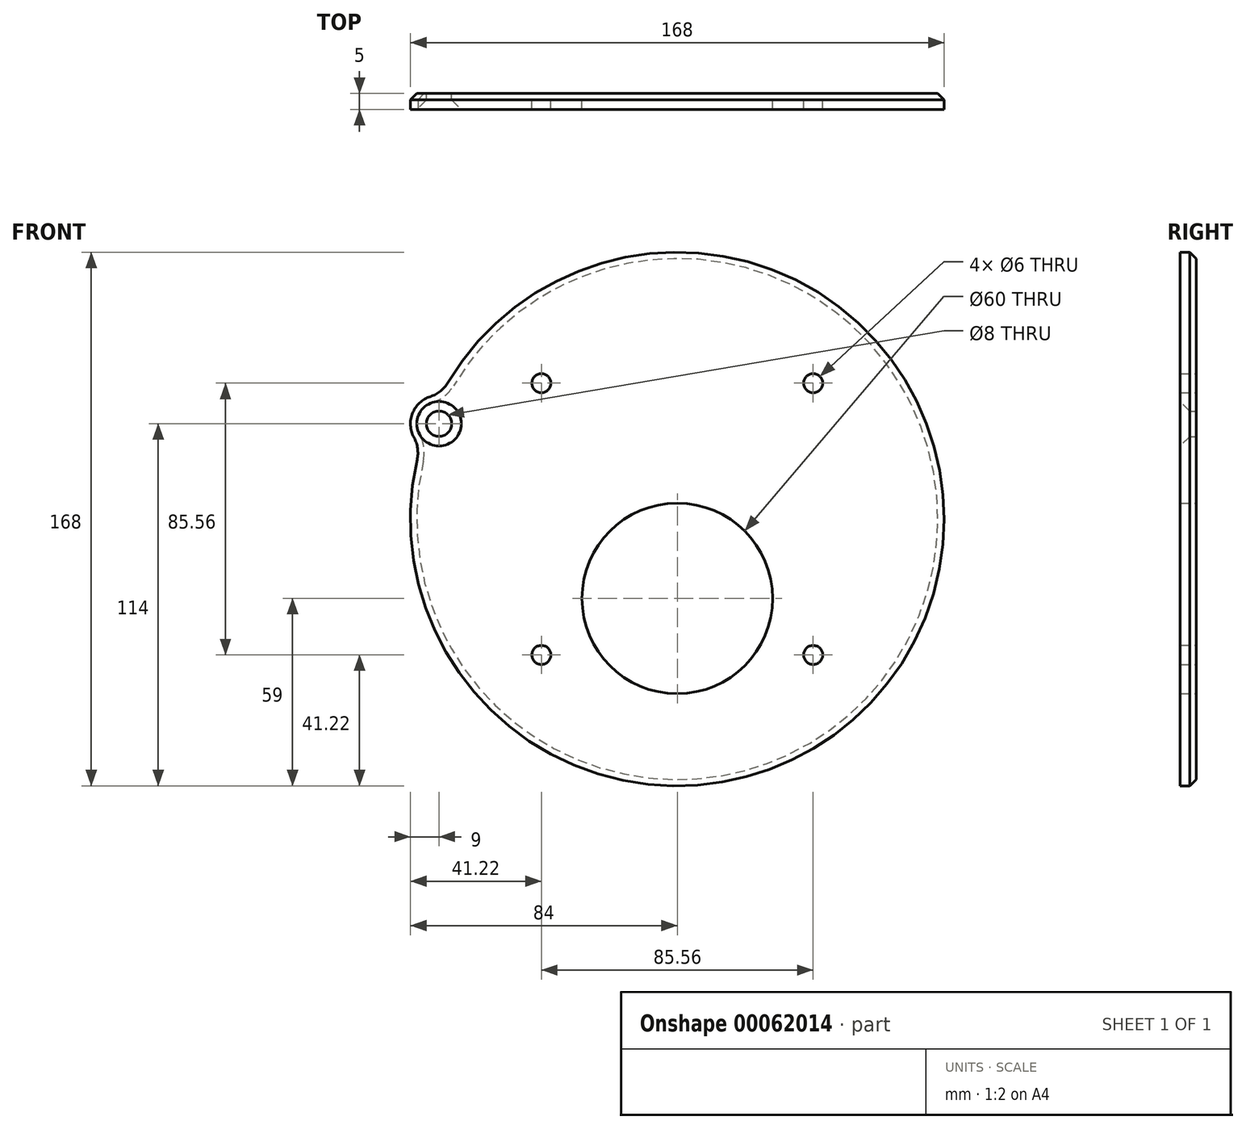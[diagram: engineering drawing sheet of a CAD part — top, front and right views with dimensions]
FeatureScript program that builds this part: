
annotation { "Feature Type Name" : "Feature", "Feature Type Description" : "" }
export const myFeature = defineFeature(function(context is Context, id is Id, definition is map)
    precondition{}
    {
        {
            var Q0;
            Q0=qCreatedBy(makeId("Front.planeOp"),FACE);
            var sketch = newSketch(context, id + "F0", { "sketchPlane" : qUnion([Q0])});
            skCircle(sketch, "E0", {"center": v(0, 0) * mm, "radius": 81 * mm, "construction": true});
            skCircle(sketch, "E1", {"center": v(0, 0) * mm, "radius": 63.5 * mm, "construction": true});
            skCircle(sketch, "E2", {"center": v(0, -25) * mm, "radius": 30 * mm});
            skLineSegment(sketch, "E3", {"start": v(0, 0) * mm, "end": v(-75, 30) * mm, "construction": true});
            skCircle(sketch, "E4", {"center": v(-75, 30) * mm, "radius": 4 * mm});
            skArc(sketch, "E5", {"start": v(-80.76, 23.09) * mm, "mid": v(78, -31.2) * mm, "end": v(-74.4, 38.98) * mm});
            skArc(sketch, "E6", {"start": v(-74.4, 38.98) * mm, "mid": v(-83.36, 33.34) * mm, "end": v(-80.76, 23.09) * mm});
            skCircle(sketch, "E7", {"center": v(0, 0) * mm, "radius": 60.5 * mm, "construction": true});
            skCircle(sketch, "E8", {"center": v(42.78, -42.78) * mm, "radius": 3 * mm});
            skCircle(sketch, "E9", {"center": v(-42.78, -42.78) * mm, "radius": 3 * mm});
            skCircle(sketch, "E10", {"center": v(42.78, 42.78) * mm, "radius": 3 * mm});
            skLineSegment(sketch, "E11", {"start": v(-42.78, 42.78) * mm, "end": v(0, 0) * mm, "construction": true});
            skLineSegment(sketch, "E12", {"start": v(42.78, 42.78) * mm, "end": v(0, 0) * mm, "construction": true});
            skLineSegment(sketch, "E13", {"start": v(0, 0) * mm, "end": v(42.78, -42.78) * mm, "construction": true});
            skCircle(sketch, "E14", {"center": v(-42.78, 42.78) * mm, "radius": 3 * mm});
            skCircle(sketch, "E15", {"center": v(0, 60.5) * mm, "radius": 3 * mm, "construction": true});
            skSolve(sketch);
        }
        {
            var Q0;
            Q0 = qSketchRegion(id + "F0", true);
            extrude(context, id + "F1", {"entities" : qUnion([Q0]), "depth" : 5 * mm});
        }
        {
            var Q0;
            {var subQ0=sQuery(id+"F0.wireOp",EDGE,"E6");var subQ1=sQuery(id+"F0.wireOp",EDGE,"E5");Q0=makeQuery(id+"F1.opExtrude","SWEPT_EDGE",EDGE,{"disambiguationData":[OSD([subQ1,subQ0]),TDD([makeQuery(id+"F0.imprint","INTERSECT",VERTEX,{"disambiguationData":[OD(1.0)],"derivedFrom":[subQ1,subQ0]})])]});}
            var Q1;
            {var subQ0=sQuery(id+"F0.wireOp",EDGE,"E6");var subQ1=sQuery(id+"F0.wireOp",EDGE,"E5");Q1=makeQuery(id+"F1.opExtrude","SWEPT_EDGE",EDGE,{"disambiguationData":[OSD([subQ1,subQ0]),TDD([makeQuery(id+"F0.imprint","INTERSECT",VERTEX,{"disambiguationData":[OD(0.0)],"derivedFrom":[subQ1,subQ0]})])]});}
            fillet(context, id + "F2", {"entities" : qUnion([Q0, Q1]), "radius" : 10 * mm, "tangentPropagation" : true, "allowEdgeOverflow" : false});
        }
        {
            var Q0;
            Q0=makeQuery(id+"F1.opExtrude","CAP_EDGE",EDGE,{"disambiguationData":[OSD([sQuery(id+"F0.wireOp",EDGE,"E5")])],"isStart":true});
            chamfer(context, id + "F3", {"entities" : qUnion([Q0]), "width" : 2 * mm, "tangentPropagation" : true});
        }
        {
            var Q0;
            Q0=makeQuery(id+"F1.opExtrude","CAP_EDGE",EDGE,{"disambiguationData":[OSD([sQuery(id+"F0.wireOp",EDGE,"E4")])],"isStart":false});
            chamfer(context, id + "F4", {"entities" : qUnion([Q0]), "chamferType" : ChamferType.OFFSET_ANGLE, "width" : 3 * mm, "oppositeDirection" : false, "angle" : 45 * degree, "tangentPropagation" : true});
        }
    });
